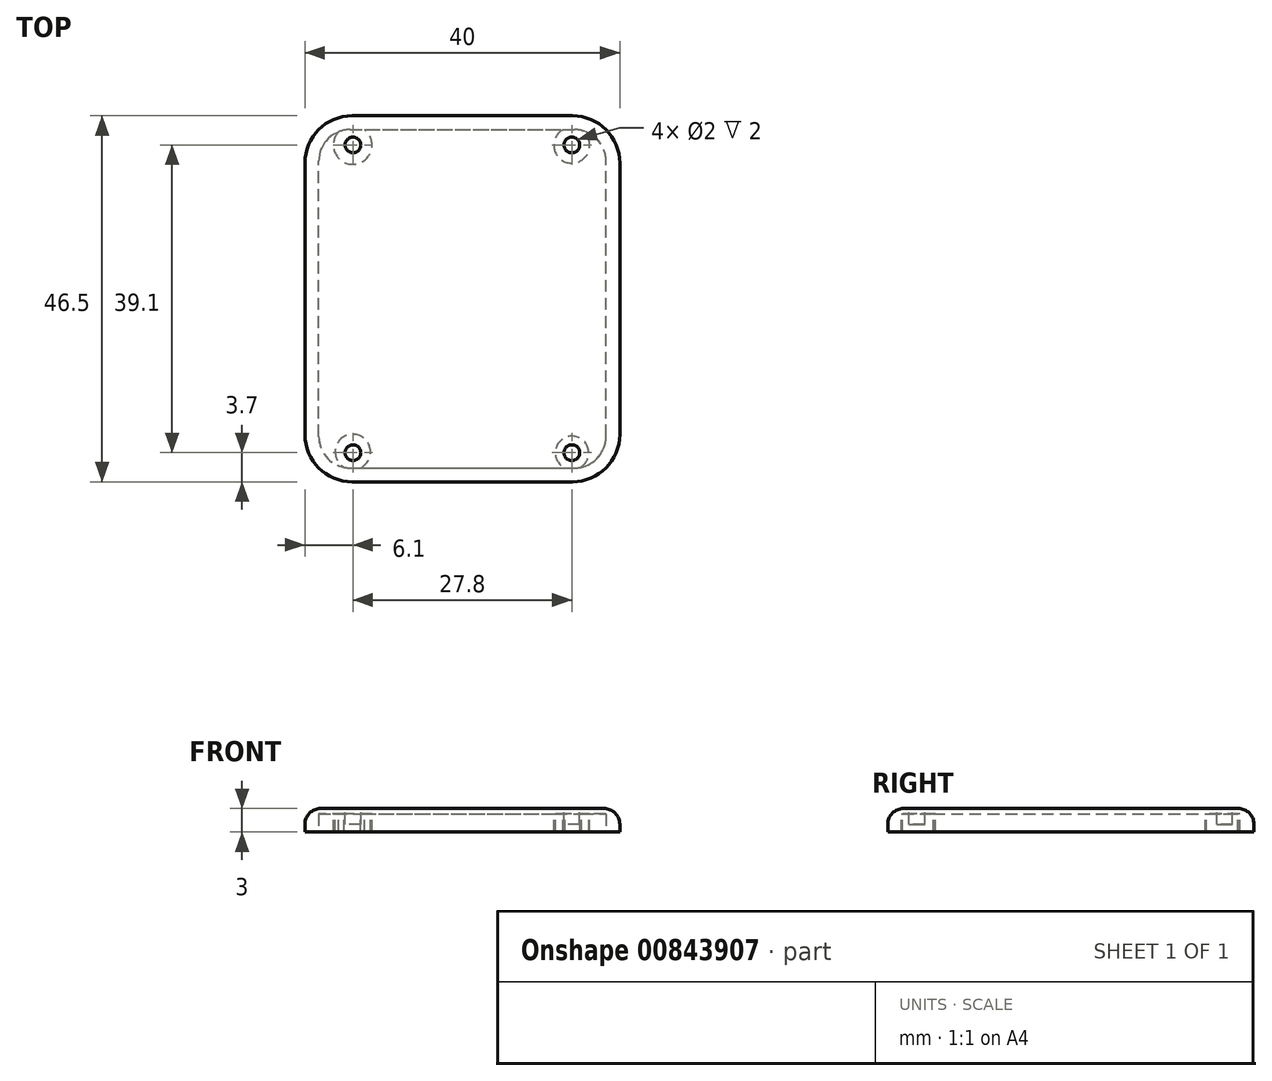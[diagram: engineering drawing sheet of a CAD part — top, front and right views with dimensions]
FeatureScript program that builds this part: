
annotation { "Feature Type Name" : "Feature", "Feature Type Description" : "" }
export const myFeature = defineFeature(function(context is Context, id is Id, definition is map)
    precondition{}
    {
        {
            var Q0;
            Q0=qCreatedBy(makeId("Top.planeOp"),FACE);
            var sketch = newSketch(context, id + "F0", { "sketchPlane" : qUnion([Q0])});
            skLineSegment(sketch, "E0.bottom", {"start": v(-14, -23.25) * mm, "end": v(14, -23.25) * mm});
            skLineSegment(sketch, "E0.top", {"start": v(-14, 23.25) * mm, "end": v(14, 23.25) * mm});
            skLineSegment(sketch, "E0.left", {"start": v(-20, -17.25) * mm, "end": v(-20, 17.25) * mm});
            skLineSegment(sketch, "E0.right", {"start": v(20, -17.25) * mm, "end": v(20, 17.25) * mm});
            skPoint(sketch, "E0.middle", {"position": v(0, 0) * mm});
            skPoint(sketch, "E1.visualSharp", {"position": v(-20, 23.25) * mm});
            skArc(sketch, "E1.filletArc", {"start": v(-14, 23.25) * mm, "mid": v(-18.24, 21.5) * mm, "end": v(-20, 17.25) * mm});
            skPoint(sketch, "E2.visualSharp", {"position": v(20, 23.25) * mm});
            skArc(sketch, "E2.filletArc", {"start": v(20, 17.25) * mm, "mid": v(18.24, 21.5) * mm, "end": v(14, 23.25) * mm});
            skPoint(sketch, "E3.visualSharp", {"position": v(20, -23.25) * mm});
            skArc(sketch, "E3.filletArc", {"start": v(14, -23.25) * mm, "mid": v(18.24, -21.5) * mm, "end": v(20, -17.25) * mm});
            skPoint(sketch, "E4.visualSharp", {"position": v(-20, -23.25) * mm});
            skArc(sketch, "E4.filletArc", {"start": v(-20, -17.25) * mm, "mid": v(-18.24, -21.5) * mm, "end": v(-14, -23.25) * mm});
            skSolve(sketch);
        }
        {
            var Q0;
            Q0=makeQuery(id+"F0.imprint","IMPRINT",FACE,{"disambiguationData":[TD([[makeQuery(id+"F0.imprint","IMPRINT",EDGE,{"derivedFrom":sQuery(id+"F0.wireOp",EDGE,"E0.bottom")}),1.0]])]});
            extrude(context, id + "F1", {"entities" : qUnion([Q0]), "depth" : 3 * mm, "offsetDistance" : 25 * mm});
        }
        {
            var Q0;
            Q0=makeQuery(id+"F1.opExtrude","CAP_FACE",FACE,{"disambiguationData":[OSD([sQuery(id+"F0.wireOp",EDGE,"E0.bottom"),sQuery(id+"F0.wireOp",EDGE,"E0.top"),sQuery(id+"F0.wireOp",EDGE,"E0.left"),sQuery(id+"F0.wireOp",EDGE,"E0.right"),sQuery(id+"F0.wireOp",EDGE,"E1.filletArc"),sQuery(id+"F0.wireOp",EDGE,"E2.filletArc"),sQuery(id+"F0.wireOp",EDGE,"E3.filletArc"),sQuery(id+"F0.wireOp",EDGE,"E4.filletArc")])],"isStart":false});
            var sketch = newSketch(context, id + "F2", { "sketchPlane" : qUnion([Q0])});
            skLineSegment(sketch, "E5.bottom", {"start": v(-13.9, -19.55) * mm, "end": v(13.9, -19.55) * mm});
            skLineSegment(sketch, "E5.top", {"start": v(-13.9, 19.55) * mm, "end": v(13.9, 19.55) * mm});
            skLineSegment(sketch, "E5.left", {"start": v(-13.9, -19.55) * mm, "end": v(-13.9, 19.55) * mm});
            skLineSegment(sketch, "E5.right", {"start": v(13.9, -19.55) * mm, "end": v(13.9, 19.55) * mm});
            skPoint(sketch, "E5.middle", {"position": v(0, 0) * mm});
            skCircle(sketch, "E6", {"center": v(13.9, 19.55) * mm, "radius": 1 * mm});
            skCircle(sketch, "E7", {"center": v(-13.9, 19.55) * mm, "radius": 1 * mm});
            skCircle(sketch, "E8", {"center": v(-13.9, -19.55) * mm, "radius": 1 * mm});
            skCircle(sketch, "E9", {"center": v(13.9, -19.55) * mm, "radius": 1 * mm});
            skSolve(sketch);
        }
        {
            var Q0;
            Q0=makeQuery(id+"F1.opExtrude","CAP_EDGE",EDGE,{"disambiguationData":[OSD([sQuery(id+"F0.wireOp",EDGE,"E0.bottom")])],"isStart":false});
            var Q1;
            Q1=makeQuery(id+"F1.opExtrude","CAP_EDGE",EDGE,{"disambiguationData":[OSD([sQuery(id+"F0.wireOp",EDGE,"E3.filletArc")])],"isStart":false});
            var Q2;
            Q2=makeQuery(id+"F1.opExtrude","CAP_EDGE",EDGE,{"disambiguationData":[OSD([sQuery(id+"F0.wireOp",EDGE,"E0.right")])],"isStart":false});
            var Q3;
            Q3=makeQuery(id+"F1.opExtrude","CAP_EDGE",EDGE,{"disambiguationData":[OSD([sQuery(id+"F0.wireOp",EDGE,"E2.filletArc")])],"isStart":false});
            var Q4;
            Q4=makeQuery(id+"F1.opExtrude","CAP_EDGE",EDGE,{"disambiguationData":[OSD([sQuery(id+"F0.wireOp",EDGE,"E0.top")])],"isStart":false});
            var Q5;
            Q5=makeQuery(id+"F1.opExtrude","CAP_EDGE",EDGE,{"disambiguationData":[OSD([sQuery(id+"F0.wireOp",EDGE,"E1.filletArc")])],"isStart":false});
            var Q6;
            Q6=makeQuery(id+"F1.opExtrude","CAP_EDGE",EDGE,{"disambiguationData":[OSD([sQuery(id+"F0.wireOp",EDGE,"E0.left")])],"isStart":false});
            var Q7;
            Q7=makeQuery(id+"F1.opExtrude","CAP_EDGE",EDGE,{"disambiguationData":[OSD([sQuery(id+"F0.wireOp",EDGE,"E4.filletArc")])],"isStart":false});
            fillet(context, id + "F3", {"entities" : qUnion([Q0, Q1, Q2, Q3, Q4, Q5, Q6, Q7]), "radius" : 2 * mm, "tangentPropagation" : true, "allowEdgeOverflow" : false});
        }
        {
            var Q0;
            Q0=makeQuery(id+"F1.opExtrude","CAP_FACE",FACE,{"disambiguationData":[OSD([sQuery(id+"F0.wireOp",EDGE,"E0.bottom"),sQuery(id+"F0.wireOp",EDGE,"E0.top"),sQuery(id+"F0.wireOp",EDGE,"E0.left"),sQuery(id+"F0.wireOp",EDGE,"E0.right"),sQuery(id+"F0.wireOp",EDGE,"E1.filletArc"),sQuery(id+"F0.wireOp",EDGE,"E2.filletArc"),sQuery(id+"F0.wireOp",EDGE,"E3.filletArc"),sQuery(id+"F0.wireOp",EDGE,"E4.filletArc")])],"isStart":true});
            var sketch = newSketch(context, id + "F4", { "sketchPlane" : qUnion([Q0])});
            skLineSegment(sketch, "E10.bottom", {"start": v(-14.24, 21.5) * mm, "end": v(14.24, 21.5) * mm});
            skLineSegment(sketch, "E10.top", {"start": v(-14.24, -21.5) * mm, "end": v(14.24, -21.5) * mm});
            skLineSegment(sketch, "E10.left", {"start": v(-18.24, 17.5) * mm, "end": v(-18.24, -17.5) * mm});
            skLineSegment(sketch, "E10.right", {"start": v(18.24, 17.5) * mm, "end": v(18.24, -17.5) * mm});
            skPoint(sketch, "E10.middle", {"position": v(0, 0) * mm});
            skPoint(sketch, "E11.visualSharp", {"position": v(18.24, 21.5) * mm});
            skArc(sketch, "E11.filletArc", {"start": v(18.24, 17.5) * mm, "mid": v(17.07, 20.32) * mm, "end": v(14.24, 21.5) * mm});
            skPoint(sketch, "E12.visualSharp", {"position": v(18.24, -21.5) * mm});
            skArc(sketch, "E12.filletArc", {"start": v(14.24, -21.5) * mm, "mid": v(17.07, -20.32) * mm, "end": v(18.24, -17.5) * mm});
            skPoint(sketch, "E13.visualSharp", {"position": v(-18.24, -21.5) * mm});
            skArc(sketch, "E13.filletArc", {"start": v(-18.24, -17.5) * mm, "mid": v(-17.07, -20.32) * mm, "end": v(-14.24, -21.5) * mm});
            skPoint(sketch, "E14.visualSharp", {"position": v(-18.24, 21.5) * mm});
            skArc(sketch, "E14.filletArc", {"start": v(-14.24, 21.5) * mm, "mid": v(-17.07, 20.32) * mm, "end": v(-18.24, 17.5) * mm});
            skSolve(sketch);
        }
        {
            var Q0;
            Q0=makeQuery(id+"F4.imprint","IMPRINT",FACE,{"disambiguationData":[TD([[makeQuery(id+"F4.imprint","IMPRINT",EDGE,{"derivedFrom":sQuery(id+"F4.wireOp",EDGE,"E10.bottom")}),-1.0]])]});
            extrude(context, id + "F5", {"entities" : qUnion([Q0]), "operationType" : NewBodyOperationType.REMOVE, "oppositeDirection" : true, "depth" : 2.3 * mm, "offsetDistance" : 25 * mm});
        }
        {
            var Q0;
            Q0=makeQuery(id+"F5.boolean.opBoolean","COPY",FACE,{"derivedFrom":makeQuery(id+"F5.opExtrude","CAP_FACE",FACE,{"disambiguationData":[OSD([sQuery(id+"F4.wireOp",EDGE,"E10.bottom"),sQuery(id+"F4.wireOp",EDGE,"E10.top"),sQuery(id+"F4.wireOp",EDGE,"E10.left"),sQuery(id+"F4.wireOp",EDGE,"E10.right"),sQuery(id+"F4.wireOp",EDGE,"E11.filletArc"),sQuery(id+"F4.wireOp",EDGE,"E12.filletArc"),sQuery(id+"F4.wireOp",EDGE,"E13.filletArc"),sQuery(id+"F4.wireOp",EDGE,"E14.filletArc")])],"isStart":false})});
            var sketch = newSketch(context, id + "F6", { "sketchPlane" : qUnion([Q0])});
            skCircle(sketch, "E15", {"center": v(-13.91, 19.46) * mm, "radius": 2.25 * mm});
            skCircle(sketch, "E16", {"center": v(13.94, 19.57) * mm, "radius": 2.12 * mm});
            skCircle(sketch, "E17", {"center": v(13.9, -19.5) * mm, "radius": 2.27 * mm});
            skCircle(sketch, "E18", {"center": v(-13.93, -19.54) * mm, "radius": 2.45 * mm});
            skSolve(sketch);
        }
        {
            var Q0;
            {var subQ0=sQuery(id+"F6.wireOp",EDGE,"E18");var subQ1=makeQuery(id+"F5.boolean.opBoolean","COPY",EDGE,{"derivedFrom":makeQuery(id+"F5.opExtrude","CAP_EDGE",EDGE,{"disambiguationData":[OSD([sQuery(id+"F4.wireOp",EDGE,"E10.top")])],"isStart":false})});var subQ2=makeQuery(id+"F6.imprint","INTERSECT",VERTEX,{"derivedFrom":[subQ1,subQ0]});Q0=makeQuery(id+"F6.imprint","IMPRINT",FACE,{"disambiguationData":[TD([[makeQuery(id+"F6.imprint","IMPRINT",EDGE,{"disambiguationData":[TD([[subQ2,-1.0]])],"derivedFrom":subQ0}),1.0]])]});}
            var Q1;
            {var subQ0=sQuery(id+"F6.wireOp",EDGE,"E15");var subQ1=makeQuery(id+"F5.boolean.opBoolean","COPY",EDGE,{"derivedFrom":makeQuery(id+"F5.opExtrude","CAP_EDGE",EDGE,{"disambiguationData":[OSD([sQuery(id+"F4.wireOp",EDGE,"E10.bottom")])],"isStart":false})});var subQ2=makeQuery(id+"F6.imprint","INTERSECT",VERTEX,{"derivedFrom":[subQ1,subQ0]});Q1=makeQuery(id+"F6.imprint","IMPRINT",FACE,{"disambiguationData":[TD([[makeQuery(id+"F6.imprint","IMPRINT",EDGE,{"disambiguationData":[TD([[subQ2,1.0]])],"derivedFrom":subQ0}),1.0]])]});}
            var Q2;
            {var subQ0=sQuery(id+"F6.wireOp",EDGE,"E16");var subQ1=makeQuery(id+"F5.boolean.opBoolean","COPY",EDGE,{"derivedFrom":makeQuery(id+"F5.opExtrude","CAP_EDGE",EDGE,{"disambiguationData":[OSD([sQuery(id+"F4.wireOp",EDGE,"E10.bottom")])],"isStart":false})});var subQ2=makeQuery(id+"F6.imprint","INTERSECT",VERTEX,{"derivedFrom":[subQ1,subQ0]});Q2=makeQuery(id+"F6.imprint","IMPRINT",FACE,{"disambiguationData":[TD([[makeQuery(id+"F6.imprint","IMPRINT",EDGE,{"disambiguationData":[TD([[subQ2,-1.0]])],"derivedFrom":subQ0}),1.0]])]});}
            var Q3;
            {var subQ0=sQuery(id+"F6.wireOp",EDGE,"E17");var subQ1=makeQuery(id+"F5.boolean.opBoolean","COPY",EDGE,{"derivedFrom":makeQuery(id+"F5.opExtrude","CAP_EDGE",EDGE,{"disambiguationData":[OSD([sQuery(id+"F4.wireOp",EDGE,"E10.top")])],"isStart":false})});var subQ2=makeQuery(id+"F6.imprint","INTERSECT",VERTEX,{"derivedFrom":[subQ1,subQ0]});Q3=makeQuery(id+"F6.imprint","IMPRINT",FACE,{"disambiguationData":[TD([[makeQuery(id+"F6.imprint","IMPRINT",EDGE,{"disambiguationData":[TD([[subQ2,1.0]])],"derivedFrom":subQ0}),1.0]])]});}
            extrude(context, id + "F7", {"entities" : qUnion([Q0, Q1, Q2, Q3]), "operationType" : NewBodyOperationType.ADD, "depth" : 2.23 * mm, "offsetDistance" : 25 * mm});
        }
        {
            var Q0;
            {var subQ0=sQuery(id+"F2.wireOp",EDGE,"E5.left");var subQ1=sQuery(id+"F2.wireOp",EDGE,"E5.top");var subQ2=makeQuery(id+"F2.imprint","INTERSECT",VERTEX,{"derivedFrom":[subQ1,subQ0]});Q0=makeQuery(id+"F2.imprint","IMPRINT",FACE,{"disambiguationData":[TD([[makeQuery(id+"F2.imprint","IMPRINT",EDGE,{"disambiguationData":[TD([[subQ2,-1.0]])],"derivedFrom":subQ1}),1.0]])]});}
            var Q1;
            {var subQ0=sQuery(id+"F2.wireOp",EDGE,"E5.left");var subQ1=sQuery(id+"F2.wireOp",EDGE,"E5.top");var subQ2=makeQuery(id+"F2.imprint","INTERSECT",VERTEX,{"derivedFrom":[subQ1,subQ0]});Q1=makeQuery(id+"F2.imprint","IMPRINT",FACE,{"disambiguationData":[TD([[makeQuery(id+"F2.imprint","IMPRINT",EDGE,{"disambiguationData":[TD([[subQ2,-1.0]])],"derivedFrom":subQ1}),-1.0]])]});}
            var Q2;
            {var subQ0=sQuery(id+"F2.wireOp",EDGE,"E5.right");var subQ1=sQuery(id+"F2.wireOp",EDGE,"E5.top");var subQ2=makeQuery(id+"F2.imprint","INTERSECT",VERTEX,{"derivedFrom":[subQ1,subQ0]});Q2=makeQuery(id+"F2.imprint","IMPRINT",FACE,{"disambiguationData":[TD([[makeQuery(id+"F2.imprint","IMPRINT",EDGE,{"disambiguationData":[TD([[subQ2,1.0]])],"derivedFrom":subQ1}),-1.0]])]});}
            var Q3;
            {var subQ0=sQuery(id+"F2.wireOp",EDGE,"E5.right");var subQ1=sQuery(id+"F2.wireOp",EDGE,"E5.top");var subQ2=makeQuery(id+"F2.imprint","INTERSECT",VERTEX,{"derivedFrom":[subQ1,subQ0]});Q3=makeQuery(id+"F2.imprint","IMPRINT",FACE,{"disambiguationData":[TD([[makeQuery(id+"F2.imprint","IMPRINT",EDGE,{"disambiguationData":[TD([[subQ2,1.0]])],"derivedFrom":subQ1}),1.0]])]});}
            var Q4;
            {var subQ0=sQuery(id+"F2.wireOp",EDGE,"E5.right");var subQ1=sQuery(id+"F2.wireOp",EDGE,"E5.bottom");var subQ2=makeQuery(id+"F2.imprint","INTERSECT",VERTEX,{"derivedFrom":[subQ1,subQ0]});Q4=makeQuery(id+"F2.imprint","IMPRINT",FACE,{"disambiguationData":[TD([[makeQuery(id+"F2.imprint","IMPRINT",EDGE,{"disambiguationData":[TD([[subQ2,1.0]])],"derivedFrom":subQ1}),-1.0]])]});}
            var Q5;
            {var subQ0=sQuery(id+"F2.wireOp",EDGE,"E5.right");var subQ1=sQuery(id+"F2.wireOp",EDGE,"E5.bottom");var subQ2=makeQuery(id+"F2.imprint","INTERSECT",VERTEX,{"derivedFrom":[subQ1,subQ0]});Q5=makeQuery(id+"F2.imprint","IMPRINT",FACE,{"disambiguationData":[TD([[makeQuery(id+"F2.imprint","IMPRINT",EDGE,{"disambiguationData":[TD([[subQ2,1.0]])],"derivedFrom":subQ1}),1.0]])]});}
            var Q6;
            {var subQ0=sQuery(id+"F2.wireOp",EDGE,"E5.left");var subQ1=sQuery(id+"F2.wireOp",EDGE,"E5.bottom");var subQ2=makeQuery(id+"F2.imprint","INTERSECT",VERTEX,{"derivedFrom":[subQ1,subQ0]});Q6=makeQuery(id+"F2.imprint","IMPRINT",FACE,{"disambiguationData":[TD([[makeQuery(id+"F2.imprint","IMPRINT",EDGE,{"disambiguationData":[TD([[subQ2,-1.0]])],"derivedFrom":subQ1}),-1.0]])]});}
            var Q7;
            {var subQ0=sQuery(id+"F2.wireOp",EDGE,"E5.left");var subQ1=sQuery(id+"F2.wireOp",EDGE,"E5.bottom");var subQ2=makeQuery(id+"F2.imprint","INTERSECT",VERTEX,{"derivedFrom":[subQ1,subQ0]});Q7=makeQuery(id+"F2.imprint","IMPRINT",FACE,{"disambiguationData":[TD([[makeQuery(id+"F2.imprint","IMPRINT",EDGE,{"disambiguationData":[TD([[subQ2,-1.0]])],"derivedFrom":subQ1}),1.0]])]});}
            var Q8;
            Q8=sQuery(id+"F2.wireOp",EDGE,"E8");
            var Q9;
            Q9=sQuery(id+"F2.wireOp",EDGE,"E9");
            var Q10;
            Q10=sQuery(id+"F2.wireOp",EDGE,"E6");
            var Q11;
            Q11=sQuery(id+"F2.wireOp",EDGE,"E7");
            extrude(context, id + "F8", {"entities" : qUnion([Q0, Q1, Q2, Q3, Q4, Q5, Q6, Q7]), "operationType" : NewBodyOperationType.REMOVE, "surfaceEntities" : qUnion([Q8, Q9, Q10, Q11]), "oppositeDirection" : true, "depth" : 2 * mm, "offsetDistance" : 25 * mm});
        }
    });
